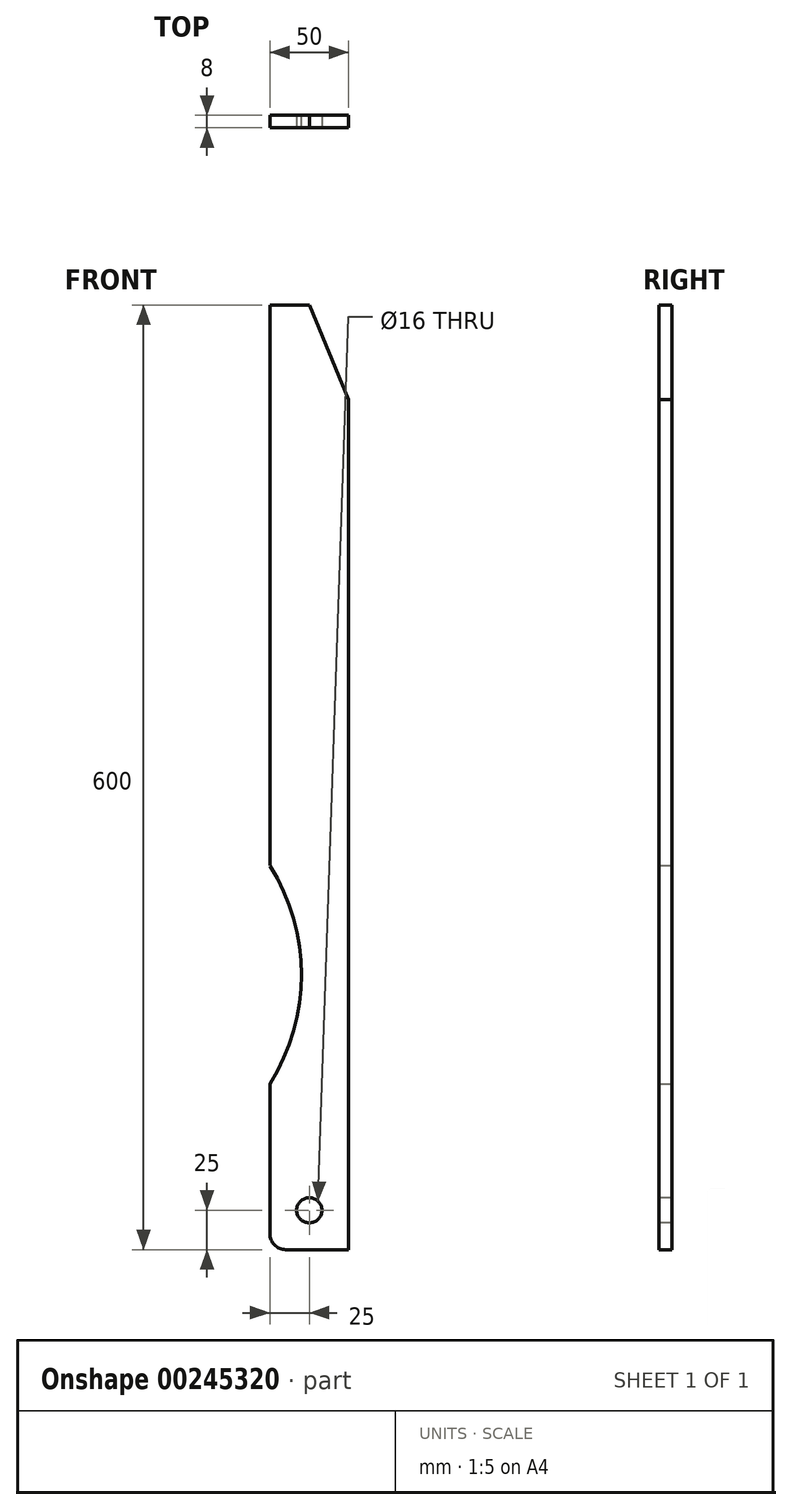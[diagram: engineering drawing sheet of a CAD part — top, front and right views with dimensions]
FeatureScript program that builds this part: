
annotation { "Feature Type Name" : "Feature", "Feature Type Description" : "" }
export const myFeature = defineFeature(function(context is Context, id is Id, definition is map)
    precondition{}
    {
        {
            var Q0;
            Q0=qCreatedBy(makeId("Front.planeOp"),FACE);
            var sketch = newSketch(context, id + "F0", { "sketchPlane" : qUnion([Q0])});
            skLineSegment(sketch, "E0.bottom", {"start": v(0, 0) * mm, "end": v(50, 0) * mm});
            skLineSegment(sketch, "E0.top", {"start": v(0, 600) * mm, "end": v(50, 600) * mm});
            skLineSegment(sketch, "E0.left", {"start": v(0, 0) * mm, "end": v(0, 105.3) * mm});
            skLineSegment(sketch, "E0.right", {"start": v(50, 0) * mm, "end": v(50, 600) * mm});
            skArc(sketch, "E1", {"start": v(0, 105.3) * mm, "mid": v(20, 174.58) * mm, "end": v(0, 243.86) * mm});
            skLineSegment(sketch, "E2.trimOffspring", {"start": v(0, 243.86) * mm, "end": v(0, 600) * mm});
            skSolve(sketch);
        }
        {
            var Q0;
            Q0=makeQuery(id+"F0.imprint","IMPRINT",FACE,{"disambiguationData":[TD([[makeQuery(id+"F0.imprint","IMPRINT",EDGE,{"derivedFrom":sQuery(id+"F0.wireOp",EDGE,"E0.bottom")}),1.0]])]});
            extrude(context, id + "F1", {"entities" : qUnion([Q0]), "depth" : 8 * mm});
        }
        {
            var Q0;
            Q0=makeQuery(id+"F1.opExtrude","CAP_FACE",FACE,{"disambiguationData":[OSD([sQuery(id+"F0.wireOp",EDGE,"E0.bottom"),sQuery(id+"F0.wireOp",EDGE,"E0.top"),sQuery(id+"F0.wireOp",EDGE,"E0.left"),sQuery(id+"F0.wireOp",EDGE,"E0.right"),sQuery(id+"F0.wireOp",EDGE,"E1"),sQuery(id+"F0.wireOp",EDGE,"E2.trimOffspring")])],"isStart":false});
            var sketch = newSketch(context, id + "F2", { "sketchPlane" : qUnion([Q0])});
            skPoint(sketch, "E3", {"position": v(25, 25) * mm});
            skSolve(sketch);
        }
        {
            var Q0;
            Q0=sQuery(id+"F2.wireOp",VERTEX,"E3");
            var Q1;
            Q1=makeQuery(id+"F1.opExtrude","SWEPT_BODY",BODY,{"disambiguationData":[OSD([sQuery(id+"F0.wireOp",EDGE,"E0.bottom"),sQuery(id+"F0.wireOp",EDGE,"E0.top"),sQuery(id+"F0.wireOp",EDGE,"E0.left"),sQuery(id+"F0.wireOp",EDGE,"E0.right"),sQuery(id+"F0.wireOp",EDGE,"E1"),sQuery(id+"F0.wireOp",EDGE,"E2.trimOffspring")])]});
            hole(context, id + "F3", {"style" : HoleStyle.SIMPLE, "endStyle" : HoleEndStyle.THROUGH, "holeDiameter" : 16 * mm, "isTappedThrough" : true, "tappedDepth" : 12 * mm, "tapClearance" : 3, "locations" : qUnion([Q0]), "scope" : qUnion([Q1])});
        }
        {
            var Q0;
            Q0=makeQuery(id+"F1.opExtrude","SWEPT_EDGE",EDGE,{"disambiguationData":[OSD([sQuery(id+"F0.wireOp",EDGE,"E0.bottom"),sQuery(id+"F0.wireOp",EDGE,"E0.left")])]});
            fillet(context, id + "F4", {"entities" : qUnion([Q0]), "radius" : 10 * mm, "tangentPropagation" : true, "allowEdgeOverflow" : false});
        }
        {
            var Q0;
            Q0=makeQuery(id+"F1.opExtrude","CAP_FACE",FACE,{"disambiguationData":[OSD([sQuery(id+"F0.wireOp",EDGE,"E0.bottom"),sQuery(id+"F0.wireOp",EDGE,"E0.top"),sQuery(id+"F0.wireOp",EDGE,"E0.left"),sQuery(id+"F0.wireOp",EDGE,"E0.right"),sQuery(id+"F0.wireOp",EDGE,"E1"),sQuery(id+"F0.wireOp",EDGE,"E2.trimOffspring")])],"isStart":false});
            var sketch = newSketch(context, id + "F5", { "sketchPlane" : qUnion([Q0])});
            skLineSegment(sketch, "E4", {"start": v(25, 600) * mm, "end": v(55.81, 525.93) * mm});
            skLineSegment(sketch, "E5", {"start": v(55.81, 525.93) * mm, "end": v(55.81, 605.28) * mm});
            skLineSegment(sketch, "E6", {"start": v(55.81, 605.28) * mm, "end": v(25, 605.28) * mm});
            skLineSegment(sketch, "E7", {"start": v(25, 605.28) * mm, "end": v(25, 600) * mm});
            skSolve(sketch);
        }
        {
            var Q0;
            {var subQ1=makeQuery(id+"F1.opExtrude","CAP_EDGE",EDGE,{"disambiguationData":[OSD([sQuery(id+"F0.wireOp",EDGE,"E0.top")])],"isStart":false});var subQ3=makeQuery(id+"F1.opExtrude","CAP_EDGE",EDGE,{"disambiguationData":[OSD([sQuery(id+"F0.wireOp",EDGE,"E0.right")])],"isStart":false});var subQ5=makeQuery(id+"F5.imprint","INTERSECT",VERTEX,{"derivedFrom":[subQ1,subQ3]});Q0=makeQuery(id+"F5.imprint","IMPRINT",FACE,{"disambiguationData":[TD([[makeQuery(id+"F5.imprint","IMPRINT",EDGE,{"disambiguationData":[TD([[subQ5,1.0]])],"derivedFrom":subQ3}),1.0]])]});}
            extrude(context, id + "F6", {"entities" : qUnion([Q0]), "operationType" : NewBodyOperationType.REMOVE, "oppositeDirection" : true, "depth" : 25 * mm});
        }
    });
